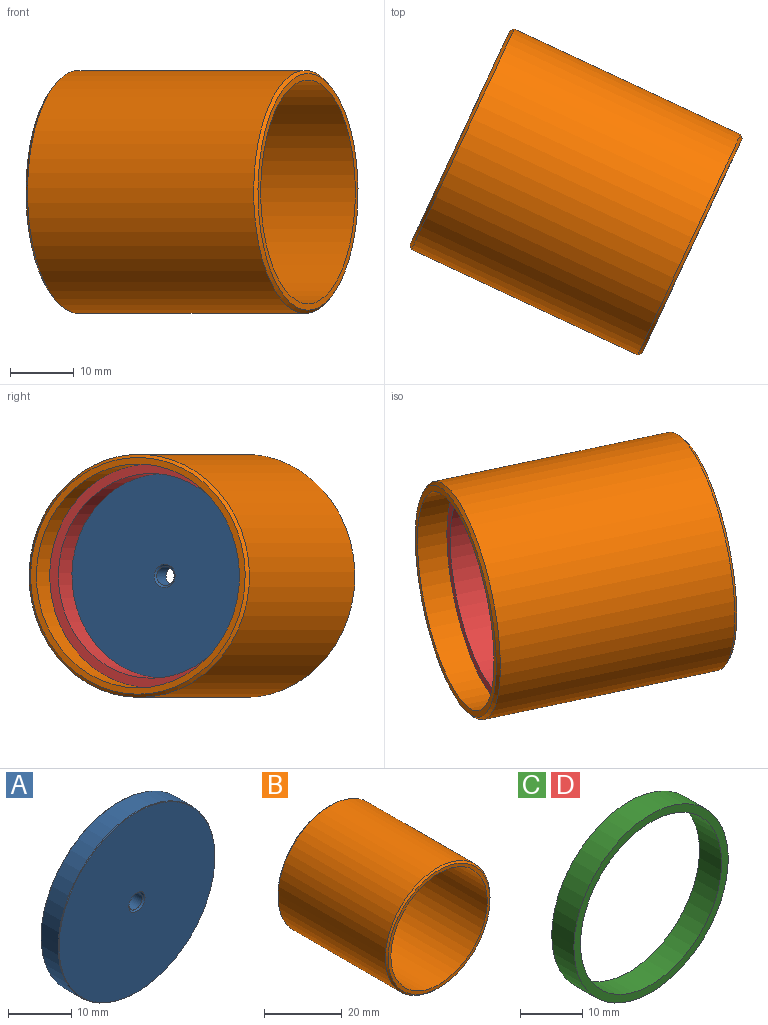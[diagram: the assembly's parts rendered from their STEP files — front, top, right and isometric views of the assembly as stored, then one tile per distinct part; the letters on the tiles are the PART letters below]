
ASSEMBLY  parts=4 mates=3
PART A: 8 faces, bbox 35x4x35 mm
  f0: cylinder r=1.5mm len=3.4mm, axis (0,-1,0), area 32mm2, adj f4,f5
  f1: cylinder r=17.5mm len=35mm, axis (0,-1,0), area 417.8mm2, adj f6,f7
  f2: plane 34.8x34.8mm, normal (0,1,0), area 941mm2, adj f4,f6
  f3: plane 34.8x34.8mm, normal (0,-1,0), area 941mm2, adj f5,f7
  f4: cone r=1.8mm half-angle=45deg, axis (0,1,0), area 4.4mm2, adj f0,f2
  f5: cone r=1.5mm half-angle=45deg, axis (0,-1,0), area 4.4mm2, adj f0,f3
  f6: cone r=17.5mm half-angle=45deg, axis (0,-1,0), area 15.5mm2, adj f1,f2
  f7: cone r=17.4mm half-angle=45deg, axis (0,1,0), area 15.5mm2, adj f1,f3
PART B: 6 faces, bbox 38x40x38 mm
  f0: cylinder r=17.5mm len=40mm, axis (0,-1,0), area 4398.2mm2, adj f2,f3
  f1: cylinder r=19mm len=39mm, axis (0,-1,0), area 4655.8mm2, adj f4,f5
  f2: plane 37x37mm, normal (0,1,0), area 113.1mm2, adj f0,f4
  f3: plane 37x37mm, normal (0,-1,0), area 113.1mm2, adj f0,f5
  f4: cone r=19mm half-angle=45deg, axis (0,-1,0), area 83.3mm2, adj f1,f2
  f5: cone r=18.5mm half-angle=45deg, axis (0,1,0), area 83.3mm2, adj f1,f3
PART C: 4 faces, bbox 35x5x35 mm
  f0: cylinder r=16mm len=32mm, axis (0,1,0), area 502.7mm2, adj f2,f3
  f1: cylinder r=17.5mm len=35mm, axis (0,1,0), area 549.8mm2, adj f2,f3
  f2: plane 35x35mm, normal (0,-1,0), area 157.9mm2, adj f0,f1
  f3: plane 35x35mm, normal (0,1,0), area 157.9mm2, adj f0,f1
PART D: same geometry as C
PLACE A rot(axis=(0,0,-1),115deg) t=(17.98,19.41,-0.06)mm fixed
PLACE B rot(axis=(0,0,-1),115deg) t=(9.01,23.59,-0.06)mm
PLACE C rot(axis=(0,0,1),65deg) t=(42.74,63.03,-0.06)mm
PLACE D rot(axis=(0,0,-1),115deg) t=(-3.15,-25.91,-0.06)mm
MATE fastened D.f1 <-> A.f1  axis (0.91,-0.42,0) through (17.98,19.41,-0.06)mm
MATE fastened C.f0 <-> A.f0  axis (-0.91,0.42,0) through (21.61,17.72,-0.06)mm
MATE fastened A.f1 <-> B.f0  axis (-0.91,0.42,0) through (18.07,19.37,-0.06)mm
